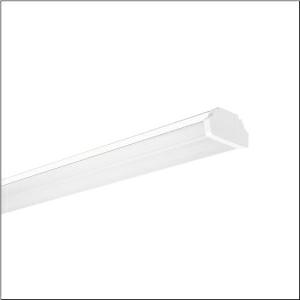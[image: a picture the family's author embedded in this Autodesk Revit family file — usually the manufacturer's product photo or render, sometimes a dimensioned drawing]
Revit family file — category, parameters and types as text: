
# Revit family: dus_r__31_mo_53bd81271v6080_96d5
name_source: partatom
category: Lighting Fixtures
units: mm (PartAtom-declared; Revit-internal decimal feet)

## family parameters
Cut with Voids When Loaded = No
Host = Face
Light Source = No
Part Type = Normal
Room Calculation Point = No
Round Connector Dimension = Use Diameter
Shared = No

## types (1)
- DUS® 31 MO (1 x LED, 7820 lm, 50.8 W, 6500K)
    Apparent Load = 51 VA
    CIE Flux Codes = 47 80 95 92 100
    Color Rendering = 80
    Color Temperature = 6500K
    Default Elevation = 1800 mm
    Description = DUS® 31 MO, luminaire insert, of sheet steel, coil coated, white, length: 1.535mm, width: 81mm, height: 90mm, 5x system unit, system units: 307mm, LED rated luminous flux: 7.820lm, light colour: 865, control gear: ON/OFF, control gear: ECG, with plug, 3-pole, with phase selection, mains connection: 220..240V, AC, 50/60Hz, rated input power: 51W, through-wiring accessed according to module size, primary optical cover: cover, of PMMA, light emission: direct distribution, primary light characteristic: symmetric, protection rating (complete): IP20, protection rating (LED compartment): IP50, insulation class (complete): insulation class I (protective earthing), certification: CE, ENEC, VDE, UKCA, impact resistance: IK03, permissible ambient temperature for indoor applications: -35..+35°C, corresponds to IFS (International Featured Standards) requirements for safety and quality in the food industry, reducing of maximum allowable ambient temperature of 5°C with ceiling mounting, packaging unit: 1 piece
    Height = 95 mm
    Lamp = 1 x LED
    Lamp Light Flux = 7820 lm
    Lamp Power = 50.8 W
    Lamp count = 1
    Length = 1535 mm
    Luminous efficacy = 154 lm/W
    Manufacturer = Siteco
    ModVariant = No
    Model = 53BD81271V6080
    Mounting Place = Ceiling
    Mounting Type = Pendant
    Number of Poles = 1
    OnlyDefault = Yes
    Power Factor = 1
    Product Name = DUS® 31 MO
    Product group = luminaire insert
    ProductGroupID = 901
    Protection Class = Protection class I
    Protection Degree = IP 20
    RLX_Detail_Level = 1
    RLX_Emergency_Light_Flux = 0 lm
    RLX_Emergency_Type = 0
    RLX_Emergency_Type_DB = No
    RlxData = <blob elided: 38457 chars, md5=b956f61c>
    Socket = socket
    Standby Power = 0 W
    System Light Flux = 7820 lm
    System Power = 51 W
    Type Comments = Product without accessories
    Type Image = l_1313537.jpg
    URL = http://relux.com
    VarID = ---
    Voltage = 0 V
    Weight = 0.00 kg
    Width = 81 mm

## geometry (parser evidence)
native form markers: Blend x4, Sweep x11
no freeform markers — native parametric forms only
